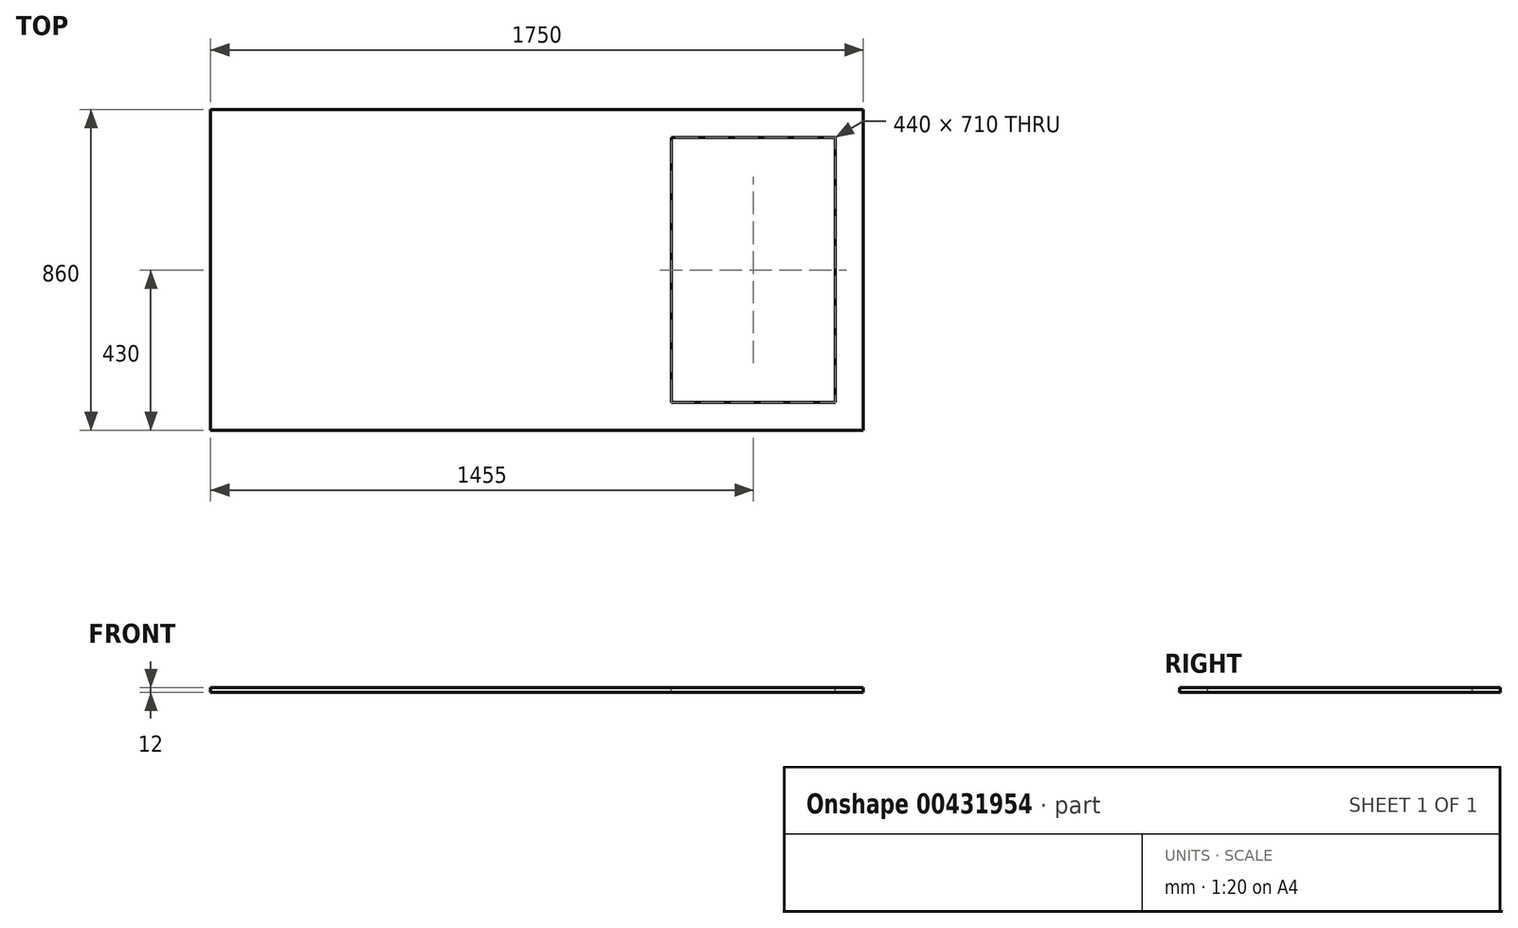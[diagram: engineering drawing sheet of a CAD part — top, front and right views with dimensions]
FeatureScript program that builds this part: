
annotation { "Feature Type Name" : "Feature", "Feature Type Description" : "" }
export const myFeature = defineFeature(function(context is Context, id is Id, definition is map)
    precondition{}
    {
        {
            var Q0;
            Q0=qCreatedBy(makeId("Top.planeOp"),FACE);
            var sketch = newSketch(context, id + "F0", { "sketchPlane" : qUnion([Q0])});
            skLineSegment(sketch, "E0.bottom", {"start": v(-875, 430) * mm, "end": v(875, 430) * mm});
            skLineSegment(sketch, "E0.top", {"start": v(-875, -430) * mm, "end": v(875, -430) * mm});
            skLineSegment(sketch, "E0.left", {"start": v(-875, 430) * mm, "end": v(-875, -430) * mm});
            skLineSegment(sketch, "E0.right", {"start": v(875, 430) * mm, "end": v(875, -430) * mm});
            skPoint(sketch, "E0.middle", {"position": v(0, 0) * mm});
            skSolve(sketch);
        }
        {
            var Q0;
            Q0 = qSketchRegion(id + "F0", true);
            extrude(context, id + "F1", {"entities" : qUnion([Q0]), "depth" : 12 * mm});
        }
        {
            var Q0;
            Q0=makeQuery(id+"F1.opExtrude","CAP_FACE",FACE,{"disambiguationData":[OSD([sQuery(id+"F0.wireOp",EDGE,"E0.bottom"),sQuery(id+"F0.wireOp",EDGE,"E0.top"),sQuery(id+"F0.wireOp",EDGE,"E0.left"),sQuery(id+"F0.wireOp",EDGE,"E0.right")])],"isStart":false});
            var sketch = newSketch(context, id + "F2", { "sketchPlane" : qUnion([Q0])});
            skLineSegment(sketch, "E1.bottom", {"start": v(800, 355) * mm, "end": v(360, 355) * mm});
            skLineSegment(sketch, "E1.top", {"start": v(800, -355) * mm, "end": v(360, -355) * mm});
            skLineSegment(sketch, "E1.left", {"start": v(800, 355) * mm, "end": v(800, -355) * mm});
            skLineSegment(sketch, "E1.right", {"start": v(360, 355) * mm, "end": v(360, -355) * mm});
            skLineSegment(sketch, "E2", {"start": v(0, 0) * mm, "end": v(360, 0) * mm, "construction": true});
            skSolve(sketch);
        }
        {
            var Q0;
            Q0 = qSketchRegion(id + "F2", true);
            extrude(context, id + "F3", {"entities" : qUnion([Q0]), "operationType" : NewBodyOperationType.REMOVE, "endBound" : BoundingType.UP_TO_NEXT, "oppositeDirection" : true, "depth" : 25 * mm});
        }
    });
